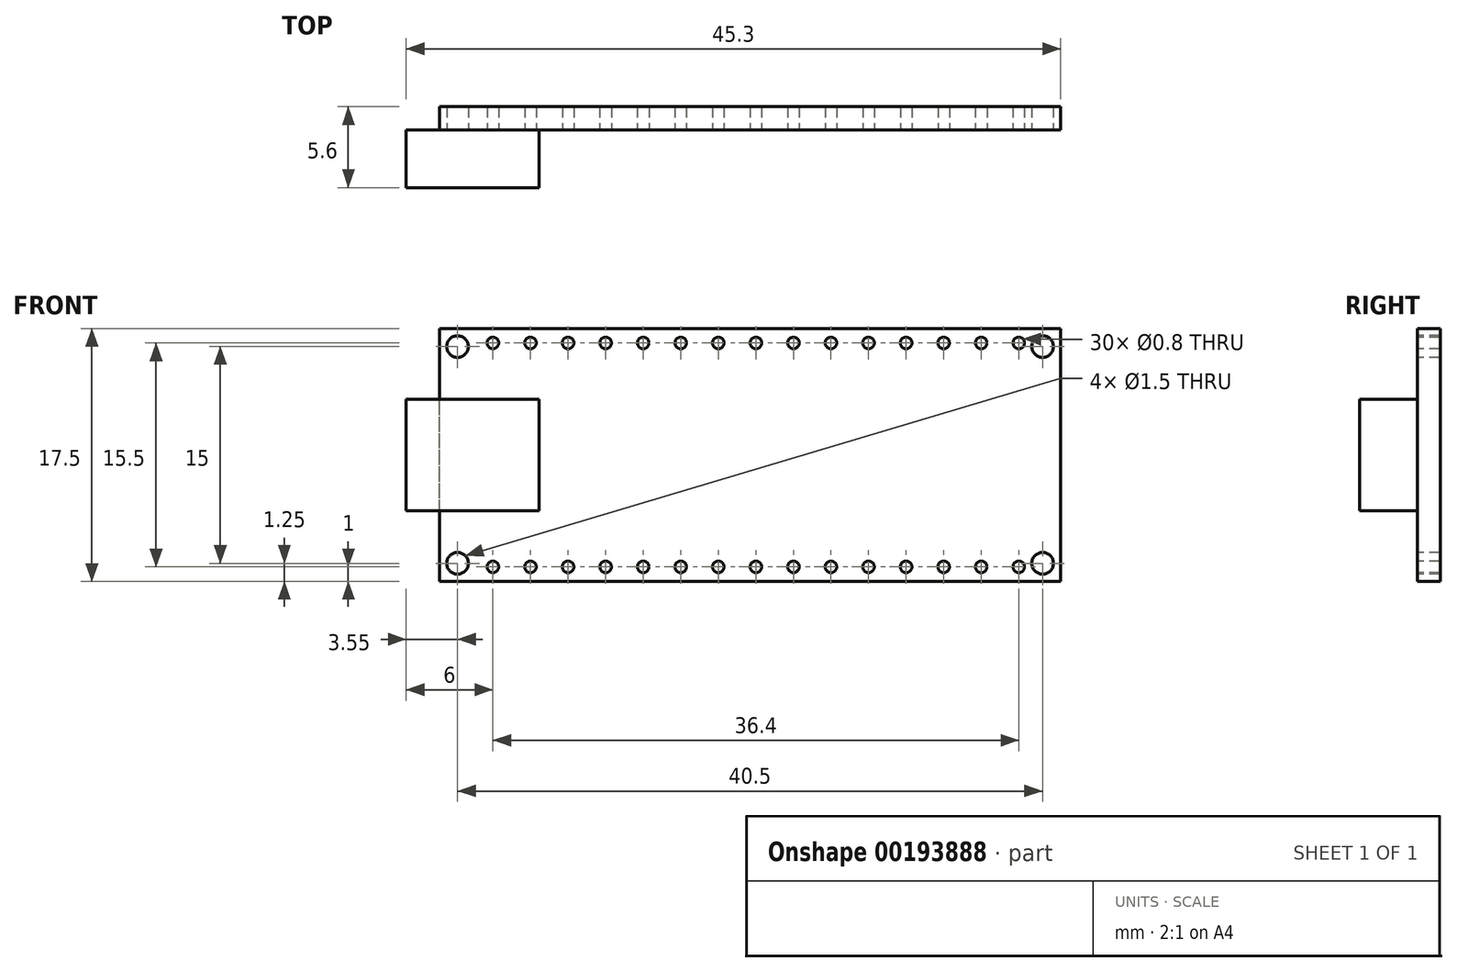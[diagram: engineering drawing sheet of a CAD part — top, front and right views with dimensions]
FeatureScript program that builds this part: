
annotation { "Feature Type Name" : "Feature", "Feature Type Description" : "" }
export const myFeature = defineFeature(function(context is Context, id is Id, definition is map)
    precondition{}
    {
        {
            var Q0;
            Q0=qCreatedBy(makeId("Front.planeOp"),FACE);
            var sketch = newSketch(context, id + "F0", { "sketchPlane" : qUnion([Q0])});
            skLineSegment(sketch, "E0.bottom", {"start": v(21.5, -8.75) * mm, "end": v(-21.5, -8.75) * mm});
            skLineSegment(sketch, "E0.top", {"start": v(21.5, 8.75) * mm, "end": v(-21.5, 8.75) * mm});
            skLineSegment(sketch, "E0.left", {"start": v(21.5, -8.75) * mm, "end": v(21.5, 8.75) * mm});
            skLineSegment(sketch, "E0.right", {"start": v(-21.5, -8.75) * mm, "end": v(-21.5, 8.75) * mm});
            skPoint(sketch, "E0.middle", {"position": v(0, 0) * mm});
            skSolve(sketch);
        }
        {
            var Q0;
            Q0 = qSketchRegion(id + "F0", true);
            extrude(context, id + "F1", {"entities" : qUnion([Q0]), "depth" : 1.6 * mm});
        }
        {
            var Q0;
            Q0=makeQuery(id+"F1.opExtrude","CAP_FACE",FACE,{"disambiguationData":[OSD([sQuery(id+"F0.wireOp",EDGE,"E0.bottom"),sQuery(id+"F0.wireOp",EDGE,"E0.top"),sQuery(id+"F0.wireOp",EDGE,"E0.left"),sQuery(id+"F0.wireOp",EDGE,"E0.right")])],"isStart":false});
            var sketch = newSketch(context, id + "F2", { "sketchPlane" : qUnion([Q0])});
            skLineSegment(sketch, "E1.bottom", {"start": v(-23.8, 3.85) * mm, "end": v(-14.6, 3.85) * mm});
            skLineSegment(sketch, "E1.top", {"start": v(-23.8, -3.85) * mm, "end": v(-14.6, -3.85) * mm});
            skLineSegment(sketch, "E1.left", {"start": v(-23.8, 3.85) * mm, "end": v(-23.8, -3.85) * mm});
            skLineSegment(sketch, "E1.right", {"start": v(-14.6, 3.85) * mm, "end": v(-14.6, -3.85) * mm});
            skSolve(sketch);
        }
        {
            var Q0;
            Q0 = qSketchRegion(id + "F2", true);
            extrude(context, id + "F3", {"entities" : qUnion([Q0]), "operationType" : NewBodyOperationType.ADD, "depth" : 4 * mm});
        }
        {
            var Q0;
            Q0=makeQuery(id+"F1.opExtrude","CAP_FACE",FACE,{"disambiguationData":[OSD([sQuery(id+"F0.wireOp",EDGE,"E0.bottom"),sQuery(id+"F0.wireOp",EDGE,"E0.top"),sQuery(id+"F0.wireOp",EDGE,"E0.left"),sQuery(id+"F0.wireOp",EDGE,"E0.right")])],"isStart":false});
            var sketch = newSketch(context, id + "F4", { "sketchPlane" : qUnion([Q0])});
            skCircle(sketch, "E2", {"center": v(-20.25, 7.5) * mm, "radius": 0.75 * mm});
            skCircle(sketch, "E3.MirrorC", {"center": v(-20.25, -7.5) * mm, "radius": 0.75 * mm});
            skCircle(sketch, "E4.MirrorC", {"center": v(20.25, 7.5) * mm, "radius": 0.75 * mm});
            skCircle(sketch, "E5.MirrorC", {"center": v(20.25, -7.5) * mm, "radius": 0.75 * mm});
            skSolve(sketch);
        }
        {
            var Q0;
            Q0 = qSketchRegion(id + "F4", true);
            extrude(context, id + "F5", {"entities" : qUnion([Q0]), "operationType" : NewBodyOperationType.REMOVE, "endBound" : BoundingType.THROUGH_ALL, "oppositeDirection" : true, "depth" : 25 * mm});
        }
        {
            var Q0;
            Q0=makeQuery(id+"F1.opExtrude","CAP_FACE",FACE,{"disambiguationData":[OSD([sQuery(id+"F0.wireOp",EDGE,"E0.bottom"),sQuery(id+"F0.wireOp",EDGE,"E0.top"),sQuery(id+"F0.wireOp",EDGE,"E0.left"),sQuery(id+"F0.wireOp",EDGE,"E0.right")])],"isStart":false});
            var sketch = newSketch(context, id + "F6", { "sketchPlane" : qUnion([Q0])});
            skCircle(sketch, "E6", {"center": v(-17.8, 7.75) * mm, "radius": 0.4 * mm});
            skCircle(sketch, "E7.1.0.0", {"center": v(-15.2, 7.75) * mm, "radius": 0.4 * mm});
            skCircle(sketch, "E7.2.0.0", {"center": v(-12.6, 7.75) * mm, "radius": 0.4 * mm});
            skCircle(sketch, "E7.3.0.0", {"center": v(-10, 7.75) * mm, "radius": 0.4 * mm});
            skCircle(sketch, "E7.4.0.0", {"center": v(-7.4, 7.75) * mm, "radius": 0.4 * mm});
            skCircle(sketch, "E7.5.0.0", {"center": v(-4.8, 7.75) * mm, "radius": 0.4 * mm});
            skCircle(sketch, "E7.6.0.0", {"center": v(-2.2, 7.75) * mm, "radius": 0.4 * mm});
            skCircle(sketch, "E7.7.0.0", {"center": v(0.4, 7.75) * mm, "radius": 0.4 * mm});
            skCircle(sketch, "E7.8.0.0", {"center": v(3, 7.75) * mm, "radius": 0.4 * mm});
            skCircle(sketch, "E7.9.0.0", {"center": v(5.6, 7.75) * mm, "radius": 0.4 * mm});
            skCircle(sketch, "E7.10.0.0", {"center": v(8.2, 7.75) * mm, "radius": 0.4 * mm});
            skCircle(sketch, "E7.11.0.0", {"center": v(10.8, 7.75) * mm, "radius": 0.4 * mm});
            skCircle(sketch, "E7.12.0.0", {"center": v(13.4, 7.75) * mm, "radius": 0.4 * mm});
            skCircle(sketch, "E7.13.0.0", {"center": v(16, 7.75) * mm, "radius": 0.4 * mm});
            skCircle(sketch, "E7.14.0.0", {"center": v(18.6, 7.75) * mm, "radius": 0.4 * mm});
            skLineSegment(sketch, "E7.direction1", {"start": v(-17.8, 7.75) * mm, "end": v(-15.2, 7.75) * mm, "construction": true});
            skLineSegment(sketch, "E8.MirrorCS", {"start": v(-17.8, -7.75) * mm, "end": v(-15.2, -7.75) * mm, "construction": true});
            skCircle(sketch, "E9.MirrorC", {"center": v(-17.8, -7.75) * mm, "radius": 0.4 * mm});
            skCircle(sketch, "E10.MirrorC", {"center": v(-15.2, -7.75) * mm, "radius": 0.4 * mm});
            skCircle(sketch, "E11.MirrorC", {"center": v(-12.6, -7.75) * mm, "radius": 0.4 * mm});
            skCircle(sketch, "E12.MirrorC", {"center": v(0.4, -7.75) * mm, "radius": 0.4 * mm});
            skCircle(sketch, "E13.MirrorC", {"center": v(-7.4, -7.75) * mm, "radius": 0.4 * mm});
            skCircle(sketch, "E14.MirrorC", {"center": v(-4.8, -7.75) * mm, "radius": 0.4 * mm});
            skCircle(sketch, "E15.MirrorC", {"center": v(-2.2, -7.75) * mm, "radius": 0.4 * mm});
            skCircle(sketch, "E16.MirrorC", {"center": v(-10, -7.75) * mm, "radius": 0.4 * mm});
            skCircle(sketch, "E17.MirrorC", {"center": v(18.6, -7.75) * mm, "radius": 0.4 * mm});
            skCircle(sketch, "E18.MirrorC", {"center": v(16, -7.75) * mm, "radius": 0.4 * mm});
            skCircle(sketch, "E19.MirrorC", {"center": v(13.4, -7.75) * mm, "radius": 0.4 * mm});
            skCircle(sketch, "E20.MirrorC", {"center": v(5.6, -7.75) * mm, "radius": 0.4 * mm});
            skCircle(sketch, "E21.MirrorC", {"center": v(3, -7.75) * mm, "radius": 0.4 * mm});
            skCircle(sketch, "E22.MirrorC", {"center": v(8.2, -7.75) * mm, "radius": 0.4 * mm});
            skCircle(sketch, "E23.MirrorC", {"center": v(10.8, -7.75) * mm, "radius": 0.4 * mm});
            skSolve(sketch);
        }
        {
            var Q0;
            Q0 = qSketchRegion(id + "F6", true);
            extrude(context, id + "F7", {"entities" : qUnion([Q0]), "operationType" : NewBodyOperationType.REMOVE, "endBound" : BoundingType.THROUGH_ALL, "oppositeDirection" : true, "depth" : 25 * mm});
        }
    });
